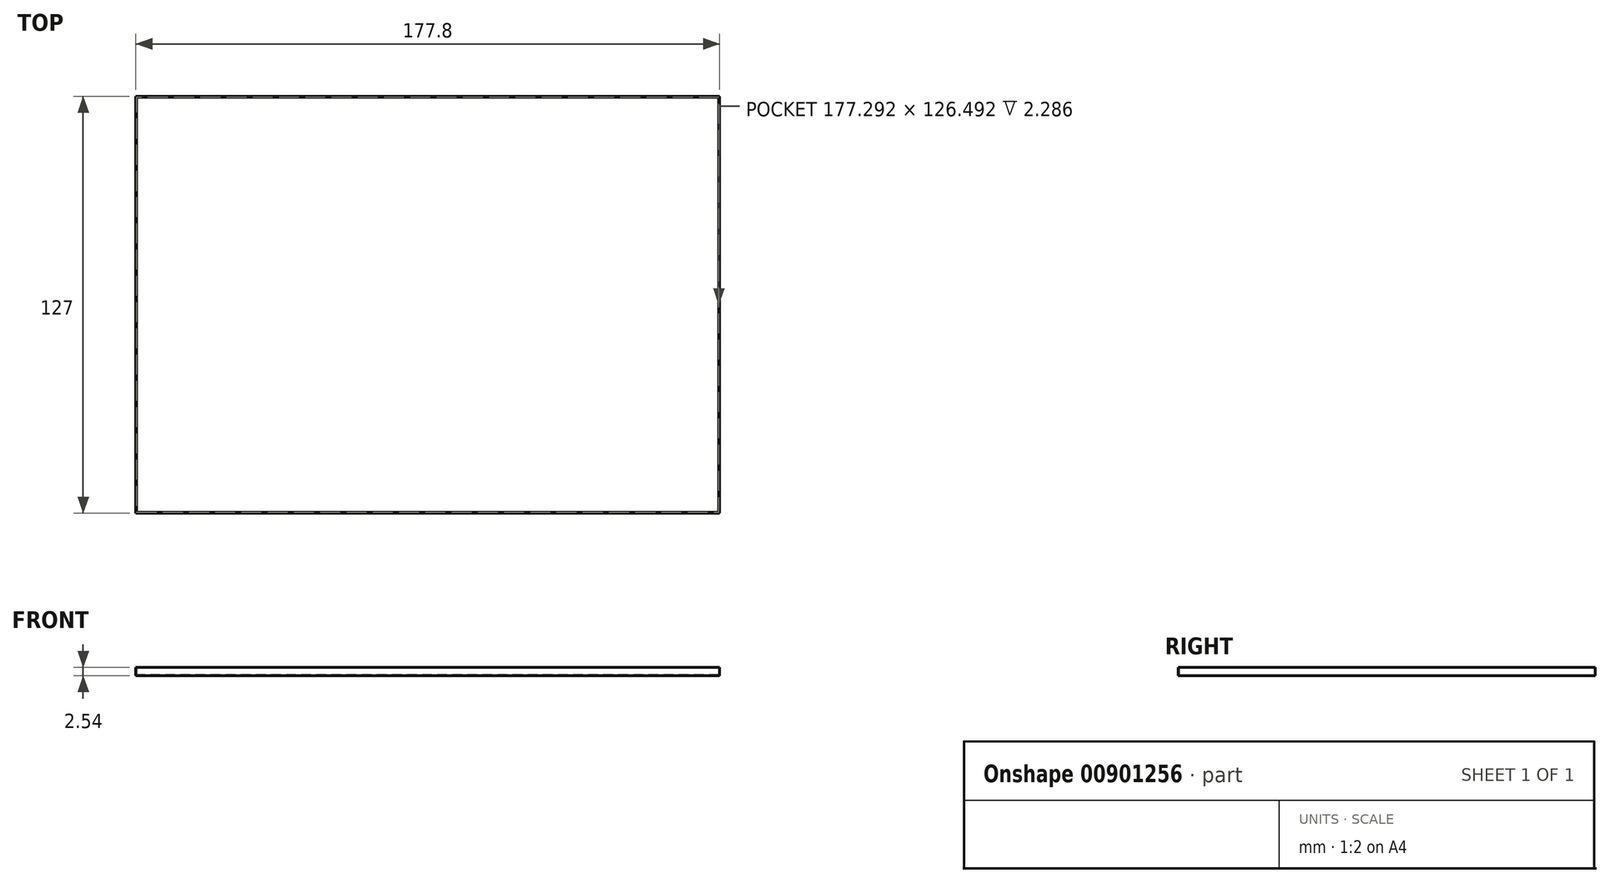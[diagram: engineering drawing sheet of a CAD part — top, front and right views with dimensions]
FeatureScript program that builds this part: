
annotation { "Feature Type Name" : "Feature", "Feature Type Description" : "" }
export const myFeature = defineFeature(function(context is Context, id is Id, definition is map)
    precondition{}
    {
        {
            var Q0;
            Q0=qCreatedBy(makeId("Top.planeOp"),FACE);
            var sketch = newSketch(context, id + "F0", { "sketchPlane" : qUnion([Q0])});
            skLineSegment(sketch, "E0.bottom", {"start": v(-76.2, 73.56) * mm, "end": v(101.6, 73.56) * mm});
            skLineSegment(sketch, "E0.top", {"start": v(-76.2, -53.44) * mm, "end": v(101.6, -53.44) * mm});
            skLineSegment(sketch, "E0.left", {"start": v(-76.2, 73.56) * mm, "end": v(-76.2, -53.44) * mm});
            skLineSegment(sketch, "E0.right", {"start": v(101.6, 73.56) * mm, "end": v(101.6, -53.44) * mm});
            skLineSegment(sketch, "E1.0", {"start": v(-75.95, 73.3) * mm, "end": v(101.35, 73.3) * mm});
            skLineSegment(sketch, "E1.1", {"start": v(-75.95, 73.3) * mm, "end": v(-75.95, -53.18) * mm});
            skLineSegment(sketch, "E1.2", {"start": v(-75.95, -53.18) * mm, "end": v(101.35, -53.18) * mm});
            skLineSegment(sketch, "E1.3", {"start": v(101.35, 73.3) * mm, "end": v(101.35, -53.18) * mm});
            skSolve(sketch);
        }
        {
            var Q0;
            Q0 = qSketchRegion(id + "F0", true);
            var Q1;
            Q1=makeQuery(id+"F0.imprint","IMPRINT",FACE,{"disambiguationData":[TD([[makeQuery(id+"F0.imprint","IMPRINT",EDGE,{"derivedFrom":sQuery(id+"F0.wireOp",EDGE,"E1.0")}),-1.0]])]});
            extrude(context, id + "F1", {"entities" : qUnion([Q0, Q1]), "depth" : 0.25 * mm, "offsetDistance" : 25.4 * mm});
        }
        {
            var Q0;
            Q0=makeQuery(id+"F0.imprint","IMPRINT",FACE,{"disambiguationData":[TD([[makeQuery(id+"F0.imprint","IMPRINT",EDGE,{"derivedFrom":sQuery(id+"F0.wireOp",EDGE,"E0.bottom")}),-1.0]])]});
            extrude(context, id + "F2", {"entities" : qUnion([Q0]), "operationType" : NewBodyOperationType.ADD, "depth" : 2.54 * mm, "offsetDistance" : 25.4 * mm});
        }
        {
            var Q0;
            Q0=makeQuery(id+"F1.opExtrude","CAP_FACE",FACE,{"disambiguationData":[OSD([sQuery(id+"F0.wireOp",EDGE,"E0.bottom"),sQuery(id+"F0.wireOp",EDGE,"E0.top"),sQuery(id+"F0.wireOp",EDGE,"E0.left"),sQuery(id+"F0.wireOp",EDGE,"E0.right")])],"isStart":false});
            var Q1;
            Q1=makeQuery(id+"F2.opExtrude","CAP_FACE",FACE,{"disambiguationData":[OSD([sQuery(id+"F0.wireOp",EDGE,"E0.bottom"),sQuery(id+"F0.wireOp",EDGE,"E0.top"),sQuery(id+"F0.wireOp",EDGE,"E0.left"),sQuery(id+"F0.wireOp",EDGE,"E0.right"),sQuery(id+"F0.wireOp",EDGE,"E1.0"),sQuery(id+"F0.wireOp",EDGE,"E1.1"),sQuery(id+"F0.wireOp",EDGE,"E1.2"),sQuery(id+"F0.wireOp",EDGE,"E1.3")])],"isStart":false});
            extrude(context, id + "F3", {"entities" : qUnion([Q0]), "endBound" : BoundingType.UP_TO_SURFACE, "depth" : 25.4 * mm, "endBoundEntityFace" : qUnion([Q1]), "offsetDistance" : 25.4 * mm});
        }
    });
